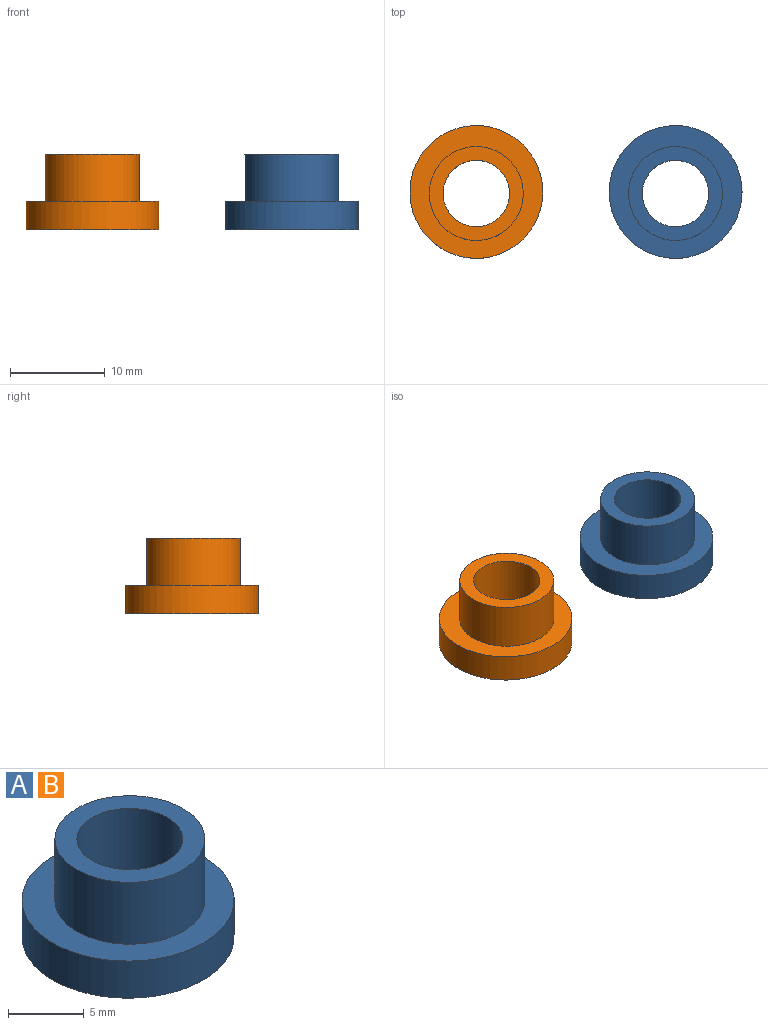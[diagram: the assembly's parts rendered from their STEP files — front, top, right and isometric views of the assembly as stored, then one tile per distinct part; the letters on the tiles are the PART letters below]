
ASSEMBLY  parts=2 mates=1
PART A: 6 faces, bbox 14x14x8 mm
  f0: cylinder r=3.5mm len=8mm, axis (0,0,-1), area 175.9mm2, adj f2,f3
  f1: cylinder r=4.95mm len=9.9mm, axis (0,0,-1), area 155.5mm2, adj f2,f5
  f2: plane 9.9x9.9mm, normal (0,0,1), area 38.5mm2, adj f0,f1
  f3: plane 14x14mm, normal (0,0,-1), area 115.5mm2, adj f0,f4
  f4: cylinder r=7mm len=14mm, axis (0,0,-1), area 131.9mm2, adj f3,f5
  f5: plane 14x14mm, normal (0,0,1), area 77mm2, adj f1,f4
PART B: same geometry as A
PLACE A t=(21,0,-3)mm
PLACE B t=(0,0,-3)mm
MATE fastened A.f1 <-> B.f5  axis (0,0,-1) through (21,0,0)mm
